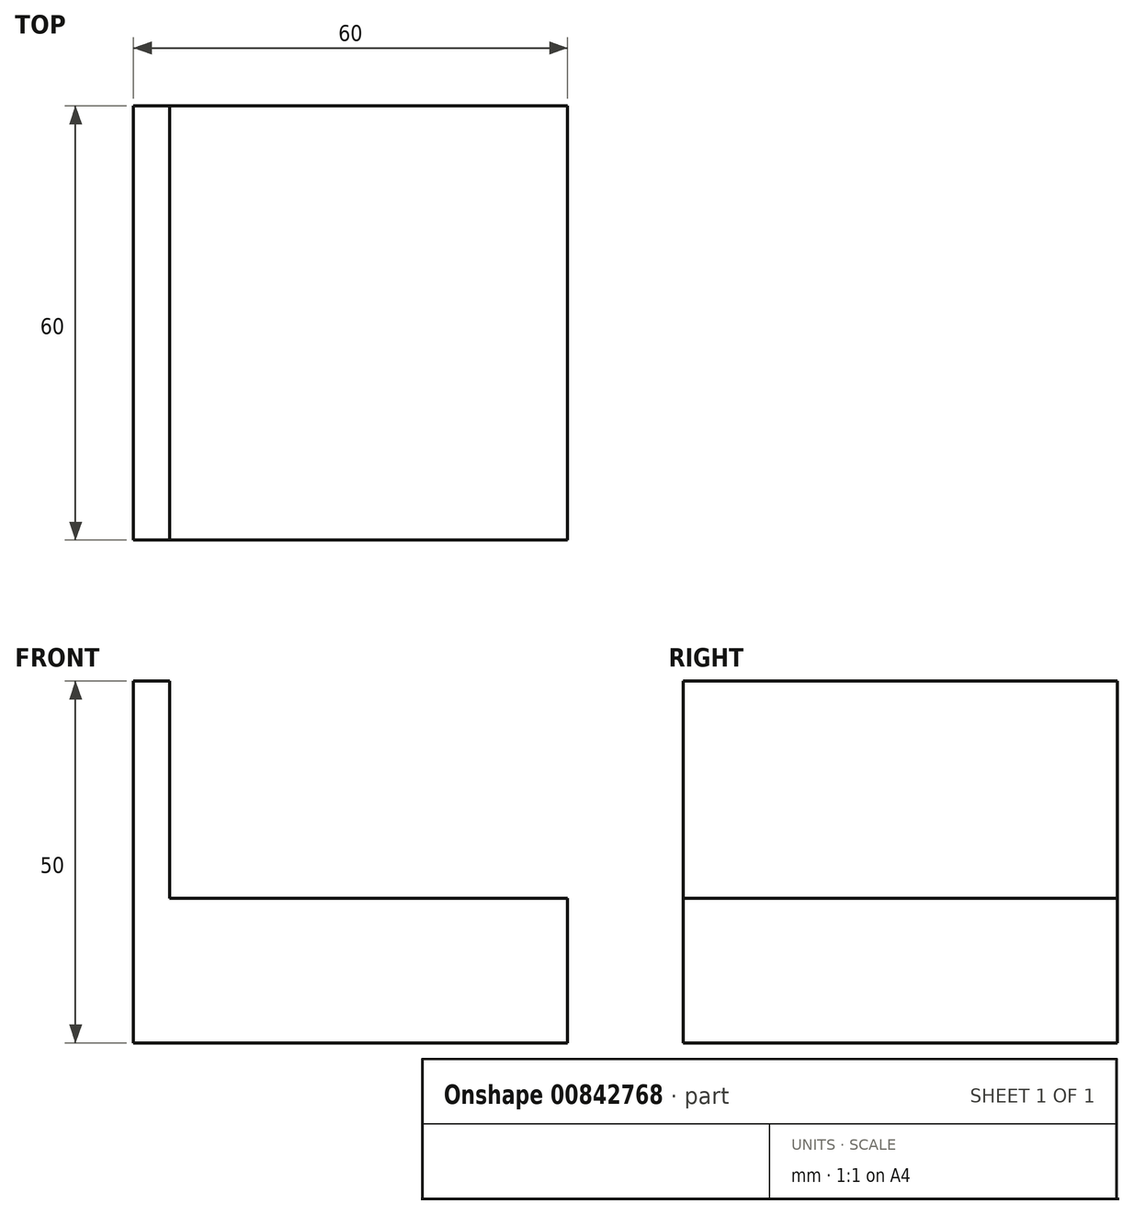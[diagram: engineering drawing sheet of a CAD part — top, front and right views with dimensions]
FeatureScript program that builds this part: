
annotation { "Feature Type Name" : "Feature", "Feature Type Description" : "" }
export const myFeature = defineFeature(function(context is Context, id is Id, definition is map)
    precondition{}
    {
        {
            var Q0;
            Q0=qCreatedBy(makeId("Front.planeOp"),FACE);
            var sketch = newSketch(context, id + "F0", { "sketchPlane" : qUnion([Q0])});
            skLineSegment(sketch, "E0.bottom", {"start": v(-30, 10) * mm, "end": v(30, 10) * mm});
            skLineSegment(sketch, "E0.top", {"start": v(-30, -10) * mm, "end": v(30, -10) * mm});
            skLineSegment(sketch, "E0.left", {"start": v(-30, 10) * mm, "end": v(-30, -10) * mm});
            skLineSegment(sketch, "E0.right", {"start": v(30, 10) * mm, "end": v(30, -10) * mm});
            skPoint(sketch, "E0.middle", {"position": v(0, 0) * mm});
            skLineSegment(sketch, "E1.bottom", {"start": v(-30, 10) * mm, "end": v(-25, 10) * mm});
            skLineSegment(sketch, "E1.top", {"start": v(-30, 40) * mm, "end": v(-25, 40) * mm});
            skLineSegment(sketch, "E1.left", {"start": v(-30, 10) * mm, "end": v(-30, 40) * mm});
            skLineSegment(sketch, "E1.right", {"start": v(-25, 10) * mm, "end": v(-25, 40) * mm});
            skSolve(sketch);
        }
        {
            var Q0;
            Q0 = qSketchRegion(id + "F0", true);
            extrude(context, id + "F1", {"entities" : qUnion([Q0]), "endBound" : BoundingType.SYMMETRIC, "depth" : 60 * mm, "offsetDistance" : 25.4 * mm});
        }
    });
